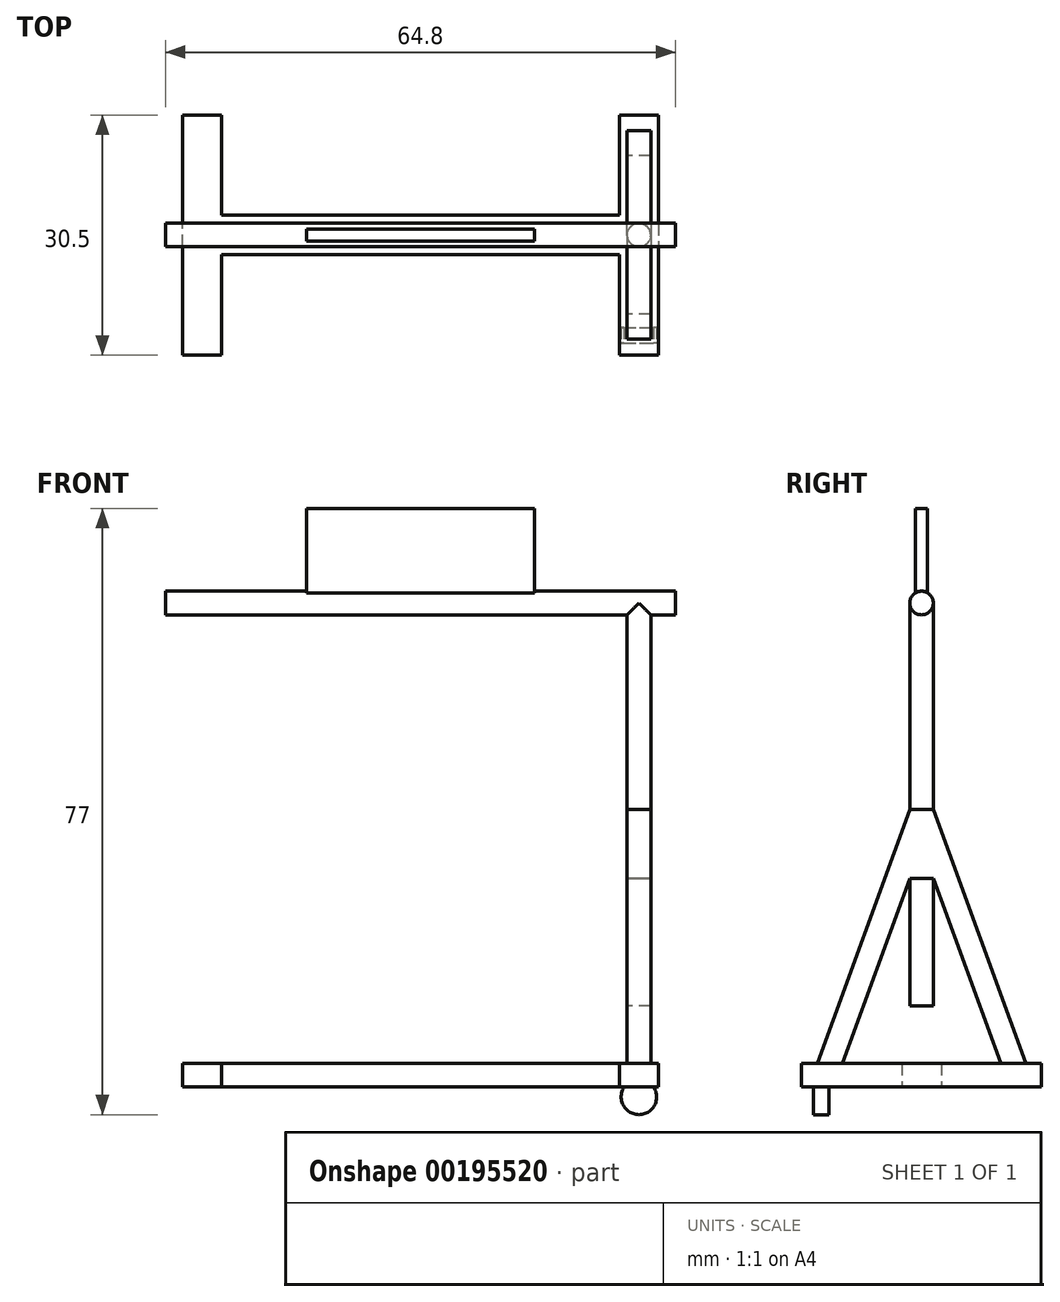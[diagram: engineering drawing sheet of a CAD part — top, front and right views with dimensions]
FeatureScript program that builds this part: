
annotation { "Feature Type Name" : "Feature", "Feature Type Description" : "" }
export const myFeature = defineFeature(function(context is Context, id is Id, definition is map)
    precondition{}
    {
        {
            var Q0;
            Q0=qCreatedBy(makeId("Top.planeOp"),FACE);
            cPlane(context, id + "F0", {"entities" : qUnion([Q0]), "cplaneType" : CPlaneType.OFFSET, "offset" : (70 / 20) * mm, "width" : 150 * mm, "height" : 150 * mm});
        }
        {
            var Q0;
            Q0=qCreatedBy(id+"F0.planeOp",FACE);
            var sketch = newSketch(context, id + "F1", { "sketchPlane" : qUnion([Q0])});
            skLineSegment(sketch, "E0", {"start": v(30.25, 0) * mm, "end": v(30.25, -15.25) * mm});
            skLineSegment(sketch, "E1", {"start": v(30.25, -15.25) * mm, "end": v(25.25, -15.25) * mm});
            skLineSegment(sketch, "E2", {"start": v(25.25, -15.25) * mm, "end": v(25.25, 2.5) * mm});
            skLineSegment(sketch, "E3", {"start": v(25.25, 2.5) * mm, "end": v(0, 2.5) * mm});
            skLineSegment(sketch, "E4.MirrorCS", {"start": v(30.25, 0) * mm, "end": v(30.25, 15.25) * mm});
            skLineSegment(sketch, "E5.MirrorCS", {"start": v(25.25, 15.25) * mm, "end": v(25.25, -2.5) * mm});
            skLineSegment(sketch, "E6.MirrorCS", {"start": v(25.25, -2.5) * mm, "end": v(0, -2.5) * mm});
            skLineSegment(sketch, "E7.MirrorCS", {"start": v(30.25, 15.25) * mm, "end": v(25.25, 15.25) * mm});
            skLineSegment(sketch, "E8.MirrorCS", {"start": v(-25.25, -2.5) * mm, "end": v(0, -2.5) * mm});
            skLineSegment(sketch, "E9.MirrorCS", {"start": v(-25.25, 15.25) * mm, "end": v(-25.25, -2.5) * mm});
            skLineSegment(sketch, "E10.MirrorCS", {"start": v(-30.25, 0) * mm, "end": v(-30.25, 15.25) * mm});
            skLineSegment(sketch, "E11.MirrorCS", {"start": v(-25.25, 2.5) * mm, "end": v(0, 2.5) * mm});
            skLineSegment(sketch, "E12.MirrorCS", {"start": v(-25.25, -15.25) * mm, "end": v(-25.25, 2.5) * mm});
            skLineSegment(sketch, "E13.MirrorCS", {"start": v(-30.25, -15.25) * mm, "end": v(-25.25, -15.25) * mm});
            skLineSegment(sketch, "E14.MirrorCS", {"start": v(-30.25, 0) * mm, "end": v(-30.25, -15.25) * mm});
            skLineSegment(sketch, "E15.MirrorCS", {"start": v(-30.25, 15.25) * mm, "end": v(-25.25, 15.25) * mm});
            skSolve(sketch);
        }
        {
            var Q0;
            {var subQ2=sQuery(id+"F1.wireOp",EDGE,"E9.MirrorCS");Q0=makeQuery(id+"F1.imprint","IMPRINT",FACE,{"disambiguationData":[TD([[makeQuery(id+"F1.imprint","IMPRINT",EDGE,{"derivedFrom":subQ2}),-1.0]])]});}
            var Q1;
            {var subQ3=sQuery(id+"F1.wireOp",EDGE,"E3");Q1=makeQuery(id+"F1.imprint","IMPRINT",FACE,{"disambiguationData":[TD([[makeQuery(id+"F1.imprint","IMPRINT",EDGE,{"derivedFrom":subQ3}),1.0]])]});}
            var Q2;
            Q2=makeQuery(id+"F1.imprint","IMPRINT",FACE,{"disambiguationData":[TD([[makeQuery(id+"F1.imprint","IMPRINT",EDGE,{"derivedFrom":sQuery(id+"F1.wireOp",EDGE,"E0")}),-1.0]])]});
            extrude(context, id + "F2", {"entities" : qUnion([Q0, Q1, Q2]), "depth" : ((40 / 20) + 1) * mm});
        }
        {
            var Q0;
            Q0=makeQuery(id+"F2.opExtrude","CAP_EDGE",EDGE,{"disambiguationData":[OSD([sQuery(id+"F1.wireOp",EDGE,"E1")])],"isStart":false});
            cPoint(context, id + "F3", {"entities" : qUnion([Q0]), "parameter" : 0.5});
        }
        {
            var Q0;
            Q0 = qCreatedBy(id + "F3" ,VERTEX);
            var Q1;
            Q1=qCreatedBy(makeId("Right.planeOp"),FACE);
            cPlane(context, id + "F4", {"entities" : qUnion([Q0, Q1]), "cplaneType" : CPlaneType.PLANE_POINT, "offset" : 25 * mm, "width" : 150 * mm, "height" : 150 * mm});
        }
        {
            var Q0;
            Q0=qCreatedBy(id+"F4.planeOp",FACE);
            var sketch = newSketch(context, id + "F5", { "sketchPlane" : qUnion([Q0])});
            skLineSegment(sketch, "E16", {"start": v(13.25, 6.5) * mm, "end": v(1.5, 38.8) * mm});
            skLineSegment(sketch, "E17", {"start": v(0, 0) * mm, "end": v(0, 26.28) * mm, "construction": true});
            skLineSegment(sketch, "E18", {"start": v(10.06, 6.5) * mm, "end": v(1.5, 30.02) * mm});
            skLineSegment(sketch, "E19", {"start": v(1.5, 30.02) * mm, "end": v(0, 30.02) * mm});
            skLineSegment(sketch, "E20", {"start": v(1.5, 38.8) * mm, "end": v(0, 38.8) * mm});
            skLineSegment(sketch, "E21", {"start": v(10.06, 6.5) * mm, "end": v(13.25, 6.5) * mm});
            skLineSegment(sketch, "E22.MirrorCS", {"start": v(-1.5, 38.8) * mm, "end": v(0, 38.8) * mm});
            skLineSegment(sketch, "E23.MirrorCS", {"start": v(-1.5, 30.02) * mm, "end": v(0, 30.02) * mm});
            skLineSegment(sketch, "E24.MirrorCS", {"start": v(-10.06, 6.5) * mm, "end": v(-13.25, 6.5) * mm});
            skLineSegment(sketch, "E25.MirrorCS", {"start": v(-10.06, 6.5) * mm, "end": v(-1.5, 30.02) * mm});
            skLineSegment(sketch, "E26.MirrorCS", {"start": v(-13.25, 6.5) * mm, "end": v(-1.5, 38.8) * mm});
            skSolve(sketch);
        }
        {
            var Q0;
            Q0=makeQuery(id+"F5.imprint","IMPRINT",FACE,{"disambiguationData":[TD([[makeQuery(id+"F5.imprint","IMPRINT",EDGE,{"derivedFrom":sQuery(id+"F5.wireOp",EDGE,"E16")}),1.0]])]});
            extrude(context, id + "F6", {"entities" : qUnion([Q0]), "operationType" : NewBodyOperationType.ADD, "endBound" : BoundingType.SYMMETRIC, "depth" : ((40 / 20) + 1) * mm});
        }
        {
            var Q0;
            Q0=qCreatedBy(makeId("Top.planeOp"),FACE);
            cPlane(context, id + "F7", {"entities" : qUnion([Q0]), "cplaneType" : CPlaneType.OFFSET, "offset" : 65 * mm, "width" : 150 * mm, "height" : 150 * mm});
        }
        {
            var Q0;
            Q0=makeQuery(id+"F6.opExtrude","SWEPT_FACE",FACE,{"disambiguationData":[OSD([sQuery(id+"F5.wireOp",EDGE,"E20"),sQuery(id+"F5.wireOp",EDGE,"E22.MirrorCS")])]});
            var sketch = newSketch(context, id + "F8", { "sketchPlane" : qUnion([Q0])});
            skCircle(sketch, "E27", {"center": v(27.75, 0) * mm, "radius": 1.5 * mm});
            skPoint(sketch, "E27.centerSnap0", {"position": v(27.75, 1.5) * mm});
            skPoint(sketch, "E27.centerSnap1", {"position": v(29.25, 0) * mm});
            skSolve(sketch);
        }
        {
            var Q0;
            {var subQ0=sQuery(id+"F8.wireOp",EDGE,"E27");var subQ1=sQuery(id+"F5.wireOp",EDGE,"E20");var subQ2=makeQuery(id+"F8.imprint","INTERSECT",VERTEX,{"derivedFrom":[makeQuery(id+"F6.opExtrude","SWEPT_EDGE",EDGE,{"disambiguationData":[OSD([sQuery(id+"F5.wireOp",EDGE,"E16"),subQ1])]}),subQ0]});Q0=makeQuery(id+"F8.imprint","IMPRINT",FACE,{"disambiguationData":[TD([[makeQuery(id+"F8.imprint","IMPRINT",EDGE,{"disambiguationData":[TD([[subQ2,1.0]])],"derivedFrom":subQ0}),1.0]])]});}
            var Q1;
            Q1=qCreatedBy(id+"F7.planeOp",FACE);
            extrude(context, id + "F9", {"entities" : qUnion([Q0]), "operationType" : NewBodyOperationType.ADD, "endBound" : BoundingType.UP_TO_SURFACE, "endBoundEntityFace" : qUnion([Q1]), "depth" : (375 / 20) * mm, "hasSecondDirection" : true, "secondDirectionOppositeDirection" : true, "secondDirectionDepth" : 25 * mm});
        }
        {
            var Q0;
            Q0=qCreatedBy(makeId("Right.planeOp"),FACE);
            var sketch = newSketch(context, id + "F10", { "sketchPlane" : qUnion([Q0])});
            skCircle(sketch, "E28", {"center": v(0, 65) * mm, "radius": 1.5 * mm});
            skLineSegment(sketch, "E29.0.0", {"start": v(-1.5, 65) * mm, "end": v(1.5, 65) * mm, "construction": true});
            skSolve(sketch);
        }
        {
            var Q0;
            Q0=makeQuery(id+"F10.imprint","IMPRINT",FACE,{"disambiguationData":[TD([[makeQuery(id+"F10.imprint","IMPRINT",EDGE,{"derivedFrom":sQuery(id+"F10.wireOp",EDGE,"E28")}),1.0]])]});
            extrude(context, id + "F11", {"entities" : qUnion([Q0]), "operationType" : NewBodyOperationType.ADD, "endBound" : BoundingType.SYMMETRIC, "depth" : (1296 / 20) * mm});
        }
        {
            var Q0;
            Q0=makeQuery(id+"F2.opExtrude","SWEPT_FACE",FACE,{"disambiguationData":[OSD([sQuery(id+"F1.wireOp",EDGE,"E1")])]});
            cPlane(context, id + "F12", {"entities" : qUnion([Q0]), "cplaneType" : CPlaneType.OFFSET, "offset" : 1.5 * mm, "oppositeDirection" : true, "width" : 150 * mm, "height" : 150 * mm});
        }
        {
            var Q0;
            Q0=qCreatedBy(id+"F12.planeOp",FACE);
            var sketch = newSketch(context, id + "F13", { "sketchPlane" : qUnion([Q0])});
            skCircle(sketch, "E30", {"center": v(27.75, 2.25) * mm, "radius": 2.25 * mm});
            skSolve(sketch);
        }
        {
            var Q0;
            Q0=makeQuery(id+"F13.imprint","IMPRINT",FACE,{"disambiguationData":[TD([[makeQuery(id+"F13.imprint","IMPRINT",EDGE,{"derivedFrom":sQuery(id+"F13.wireOp",EDGE,"E30")}),1.0]])]});
            extrude(context, id + "F14", {"entities" : qUnion([Q0]), "operationType" : NewBodyOperationType.ADD, "oppositeDirection" : true, "depth" : 2 * mm});
        }
        {
            var Q0;
            Q0=qCreatedBy(makeId("Front.planeOp"),FACE);
            var sketch = newSketch(context, id + "F15", { "sketchPlane" : qUnion([Q0])});
            skLineSegment(sketch, "E31.bottom", {"start": v(14.5, 66) * mm, "end": v(-14.5, 66) * mm});
            skLineSegment(sketch, "E31.top", {"start": v(14.5, 77) * mm, "end": v(-14.5, 77) * mm});
            skLineSegment(sketch, "E31.left", {"start": v(14.5, 66) * mm, "end": v(14.5, 77) * mm});
            skLineSegment(sketch, "E31.right", {"start": v(-14.5, 66) * mm, "end": v(-14.5, 77) * mm});
            skPoint(sketch, "E31.middle", {"position": v(0, 71.5) * mm});
            skLineSegment(sketch, "E32.0", {"start": v(32.4, 66.5) * mm, "end": v(32.4, 63.5) * mm, "construction": true});
            skSolve(sketch);
        }
        {
            var Q0;
            Q0=makeQuery(id+"F15.imprint","IMPRINT",FACE,{"disambiguationData":[TD([[makeQuery(id+"F15.imprint","IMPRINT",EDGE,{"derivedFrom":sQuery(id+"F15.wireOp",EDGE,"E31.bottom")}),-1.0]])]});
            extrude(context, id + "F16", {"entities" : qUnion([Q0]), "operationType" : NewBodyOperationType.ADD, "endBound" : BoundingType.SYMMETRIC, "depth" : 1.5 * mm});
        }
    });
